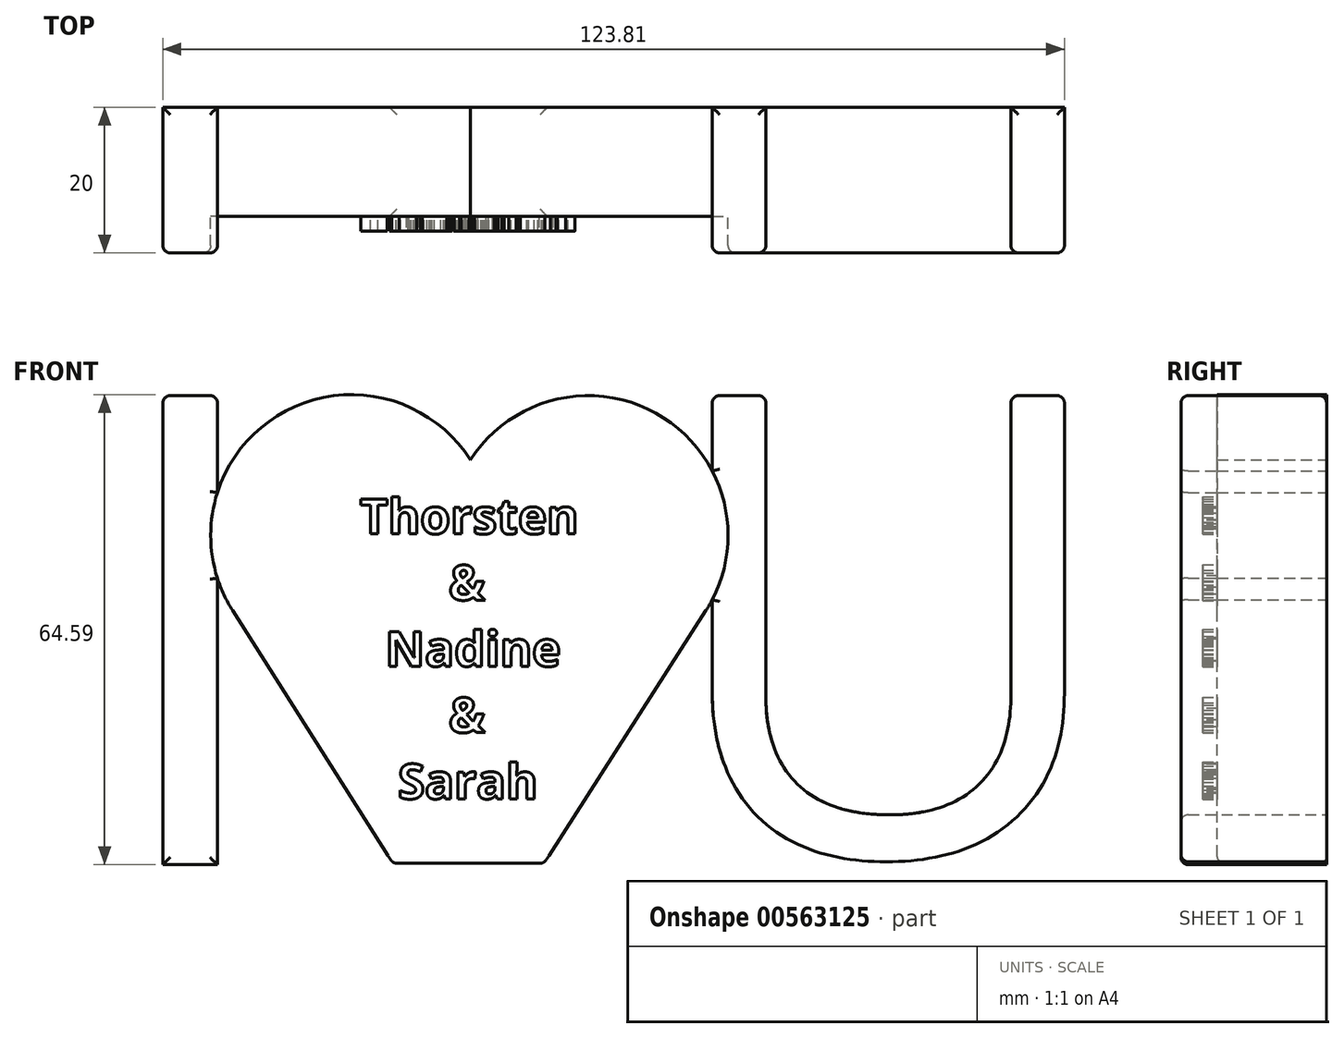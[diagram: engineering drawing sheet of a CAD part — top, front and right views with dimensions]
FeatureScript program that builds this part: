
annotation { "Feature Type Name" : "Feature", "Feature Type Description" : "" }
export const myFeature = defineFeature(function(context is Context, id is Id, definition is map)
    precondition{}
    {
        {
            var Q0;
            Q0=qCreatedBy(makeId("Front.planeOp"),FACE);
            var sketch = newSketch(context, id + "F0", { "sketchPlane" : qUnion([Q0])});
            skLineSegment(sketch, "E0", {"start": v(-10.66, 0.2) * mm, "end": v(-32.66, 34.9) * mm});
            skLineSegment(sketch, "E1", {"start": v(10.12, 0.2) * mm, "end": v(32.34, 34.9) * mm});
            skArc(sketch, "E2", {"start": v(0, 55.6) * mm, "mid": v(-26.68, 61.59) * mm, "end": v(-32.66, 34.9) * mm});
            skArc(sketch, "E3", {"start": v(32.34, 34.9) * mm, "mid": v(26.52, 61.43) * mm, "end": v(0, 55.6) * mm});
            skLineSegment(sketch, "E4", {"start": v(-10.66, 0.2) * mm, "end": v(10.12, 0.2) * mm});
            skText(sketch, "E5", { "text": "I\n", "fontName": "OpenSans-Regular.ttf"});
            skPoint(sketch, "E6.orphan", {"position": v(0, 34.9) * mm});
            skText(sketch, "E7", { "text": "U", "fontName": "OpenSans-Regular.ttf"});
            const initialGuessF0  = {"E5": [-0.0511, 0, 1, 0, 0.065], "E7": [0.02517, 0.00127, 1, 0, 0.06373]};
            skSetInitialGuess(sketch, initialGuessF0);
            skSolve(sketch);
        }
        {
            var Q0;
            Q0 = qSketchRegion(id + "F0", true);
            extrude(context, id + "F1", {"entities" : qUnion([Q0]), "depth" : 15 * mm, "offsetDistance" : 25 * mm});
        }
        {
            var Q0;
            Q0=qCreatedBy(makeId("Front.planeOp"),FACE);
            var sketch = newSketch(context, id + "F2", { "sketchPlane" : qUnion([Q0])});
            skText(sketch, "E8", { "text": "Thorsten\n       &\n  Nadine\n       &\n   Sarah", "fontName": "OpenSans-Bold.ttf"});
            const initialGuessF2  = {"E8": [-0.01517, 0.04546, 1, 0, 0.00482]};
            skSetInitialGuess(sketch, initialGuessF2);
            skSolve(sketch);
        }
        {
            var Q0;
            Q0 = qSketchRegion(id + "F2", true);
            extrude(context, id + "F3", {"entities" : qUnion([Q0]), "operationType" : NewBodyOperationType.ADD, "depth" : 17 * mm, "offsetDistance" : 25 * mm});
        }
        {
            var Q0;
            Q0=makeQuery(id+"F1.opExtrude","SWEPT_EDGE",EDGE,{"disambiguationData":[OSD([sQuery(id+"F0.wireOp",EDGE,"E5.sketch_text.stroke-1"),sQuery(id+"F0.wireOp",EDGE,"E5.sketch_text.stroke-2")])]});
            var Q1;
            Q1=makeQuery(id+"F1.opExtrude","SWEPT_EDGE",EDGE,{"disambiguationData":[OSD([sQuery(id+"F0.wireOp",EDGE,"E5.sketch_text.stroke-0"),sQuery(id+"F0.wireOp",EDGE,"E5.sketch_text.stroke-1")])]});
            var Q2;
            Q2=makeQuery(id+"F1.opExtrude","SWEPT_EDGE",EDGE,{"disambiguationData":[OSD([sQuery(id+"F0.wireOp",EDGE,"28eaa01f-b16d-456c-9d8f-c29722bd80aa.sketch_text.stroke-0"),sQuery(id+"F0.wireOp",EDGE,"28eaa01f-b16d-456c-9d8f-c29722bd80aa.sketch_text.stroke-13")])]});
            var Q3;
            Q3=makeQuery(id+"F1.opExtrude","SWEPT_EDGE",EDGE,{"disambiguationData":[OSD([sQuery(id+"F0.wireOp",EDGE,"28eaa01f-b16d-456c-9d8f-c29722bd80aa.sketch_text.stroke-12"),sQuery(id+"F0.wireOp",EDGE,"28eaa01f-b16d-456c-9d8f-c29722bd80aa.sketch_text.stroke-13")])]});
            var Q4;
            Q4=makeQuery(id+"F1.opExtrude","SWEPT_EDGE",EDGE,{"disambiguationData":[OSD([sQuery(id+"F0.wireOp",EDGE,"28eaa01f-b16d-456c-9d8f-c29722bd80aa.sketch_text.stroke-6"),sQuery(id+"F0.wireOp",EDGE,"28eaa01f-b16d-456c-9d8f-c29722bd80aa.sketch_text.stroke-7")])]});
            var Q5;
            Q5=makeQuery(id+"F1.opExtrude","SWEPT_EDGE",EDGE,{"disambiguationData":[OSD([sQuery(id+"F0.wireOp",EDGE,"28eaa01f-b16d-456c-9d8f-c29722bd80aa.sketch_text.stroke-5"),sQuery(id+"F0.wireOp",EDGE,"28eaa01f-b16d-456c-9d8f-c29722bd80aa.sketch_text.stroke-6")])]});
            var Q6;
            Q6=makeQuery(id+"F1.opExtrude","SWEPT_EDGE",EDGE,{"disambiguationData":[OSD([sQuery(id+"F0.wireOp",EDGE,"E5.sketch_text.stroke-0"),sQuery(id+"F0.wireOp",EDGE,"E5.sketch_text.stroke-3")])]});
            var Q7;
            Q7=makeQuery(id+"F1.opExtrude","SWEPT_EDGE",EDGE,{"disambiguationData":[OSD([sQuery(id+"F0.wireOp",EDGE,"E5.sketch_text.stroke-2"),sQuery(id+"F0.wireOp",EDGE,"E5.sketch_text.stroke-3")])]});
            var Q8;
            Q8=makeQuery(id+"F1.opExtrude","CAP_EDGE",EDGE,{"disambiguationData":[OSD([sQuery(id+"F0.wireOp",EDGE,"28eaa01f-b16d-456c-9d8f-c29722bd80aa.sketch_text.stroke-13")])],"isStart":true});
            var Q9;
            Q9=makeQuery(id+"F1.opExtrude","CAP_EDGE",EDGE,{"disambiguationData":[OSD([sQuery(id+"F0.wireOp",EDGE,"28eaa01f-b16d-456c-9d8f-c29722bd80aa.sketch_text.stroke-6")])],"isStart":true});
            var Q10;
            Q10=makeQuery(id+"F1.opExtrude","CAP_EDGE",EDGE,{"disambiguationData":[OSD([sQuery(id+"F0.wireOp",EDGE,"E5.sketch_text.stroke-1")])],"isStart":true});
            var Q11;
            Q11=makeQuery(id+"F1.opExtrude","CAP_EDGE",EDGE,{"disambiguationData":[OSD([sQuery(id+"F0.wireOp",EDGE,"E5.sketch_text.stroke-3")])],"isStart":true});
            fillet(context, id + "F4", {"entities" : qUnion([Q0, Q1, Q2, Q3, Q4, Q5, Q6, Q7, Q8, Q9, Q10, Q11]), "radius" : 1 * mm, "tangentPropagation" : true, "allowEdgeOverflow" : false});
        }
        {
            var Q0;
            Q0=makeQuery(id+"F0.imprint","IMPRINT",FACE,{"disambiguationData":[TD([[makeQuery(id+"F0.imprint","IMPRINT",EDGE,{"derivedFrom":sQuery(id+"F0.wireOp",EDGE,"E5.sketch_text.stroke-0")}),-1.0]])]});
            var Q1;
            Q1=makeQuery(id+"F0.imprint","IMPRINT",FACE,{"disambiguationData":[TD([[makeQuery(id+"F0.imprint","IMPRINT",EDGE,{"derivedFrom":sQuery(id+"F0.wireOp",EDGE,"E7.sketch_text.stroke-0")}),-1.0]])]});
            extrude(context, id + "F5", {"entities" : qUnion([Q0, Q1]), "operationType" : NewBodyOperationType.ADD, "depth" : 20 * mm, "offsetDistance" : 25 * mm});
        }
        {
            var Q0;
            Q0=makeQuery(id+"F5.opExtrude","CAP_FACE",FACE,{"disambiguationData":[OSD([sQuery(id+"F0.wireOp",EDGE,"E2"),sQuery(id+"F0.wireOp",EDGE,"E5.sketch_text.stroke-0"),sQuery(id+"F0.wireOp",EDGE,"E5.sketch_text.stroke-1"),sQuery(id+"F0.wireOp",EDGE,"E5.sketch_text.stroke-2"),sQuery(id+"F0.wireOp",EDGE,"E5.sketch_text.stroke-3")])],"isStart":false});
            var Q1;
            Q1=makeQuery(id+"F5.opExtrude","CAP_FACE",FACE,{"disambiguationData":[OSD([sQuery(id+"F0.wireOp",EDGE,"E3"),sQuery(id+"F0.wireOp",EDGE,"E7.sketch_text.stroke-0"),sQuery(id+"F0.wireOp",EDGE,"E7.sketch_text.stroke-1"),sQuery(id+"F0.wireOp",EDGE,"E7.sketch_text.stroke-2"),sQuery(id+"F0.wireOp",EDGE,"E7.sketch_text.stroke-3"),sQuery(id+"F0.wireOp",EDGE,"E7.sketch_text.stroke-4"),sQuery(id+"F0.wireOp",EDGE,"E7.sketch_text.stroke-5"),sQuery(id+"F0.wireOp",EDGE,"E7.sketch_text.stroke-6"),sQuery(id+"F0.wireOp",EDGE,"E7.sketch_text.stroke-7"),sQuery(id+"F0.wireOp",EDGE,"E7.sketch_text.stroke-8"),sQuery(id+"F0.wireOp",EDGE,"E7.sketch_text.stroke-9"),sQuery(id+"F0.wireOp",EDGE,"E7.sketch_text.stroke-10"),sQuery(id+"F0.wireOp",EDGE,"E7.sketch_text.stroke-11"),sQuery(id+"F0.wireOp",EDGE,"E7.sketch_text.stroke-12"),sQuery(id+"F0.wireOp",EDGE,"E7.sketch_text.stroke-13")])],"isStart":false});
            var Q2;
            Q2=makeQuery(id+"F1.opExtrude","SWEPT_FACE",FACE,{"disambiguationData":[OSD([sQuery(id+"F0.wireOp",EDGE,"E4")])]});
            var Q3;
            {var subQ0=sQuery(id+"F0.wireOp",EDGE,"E7.sketch_text.stroke-13");Q3=makeQuery(id+"F5.boolean.opBoolean","MERGE",FACE,{"derivedFrom":[makeQuery(id+"F1.opExtrude","SWEPT_FACE",FACE,{"disambiguationData":[OSD([subQ0])]}),makeQuery(id+"F5.opExtrude","SWEPT_FACE",FACE,{"disambiguationData":[OSD([subQ0])]})]});}
            var Q4;
            {var subQ0=sQuery(id+"F0.wireOp",EDGE,"E7.sketch_text.stroke-6");Q4=makeQuery(id+"F5.boolean.opBoolean","MERGE",FACE,{"derivedFrom":[makeQuery(id+"F1.opExtrude","SWEPT_FACE",FACE,{"disambiguationData":[OSD([subQ0])]}),makeQuery(id+"F5.opExtrude","SWEPT_FACE",FACE,{"disambiguationData":[OSD([subQ0])]})]});}
            var Q5;
            {var subQ0=sQuery(id+"F0.wireOp",EDGE,"E5.sketch_text.stroke-1");Q5=makeQuery(id+"F5.boolean.opBoolean","MERGE",FACE,{"derivedFrom":[makeQuery(id+"F1.opExtrude","SWEPT_FACE",FACE,{"disambiguationData":[OSD([subQ0])]}),makeQuery(id+"F5.opExtrude","SWEPT_FACE",FACE,{"disambiguationData":[OSD([subQ0])]})]});}
            fillet(context, id + "F6", {"entities" : qUnion([Q0, Q1, Q2, Q3, Q4, Q5]), "radius" : 1 * mm, "tangentPropagation" : true, "allowEdgeOverflow" : false});
        }
    });
